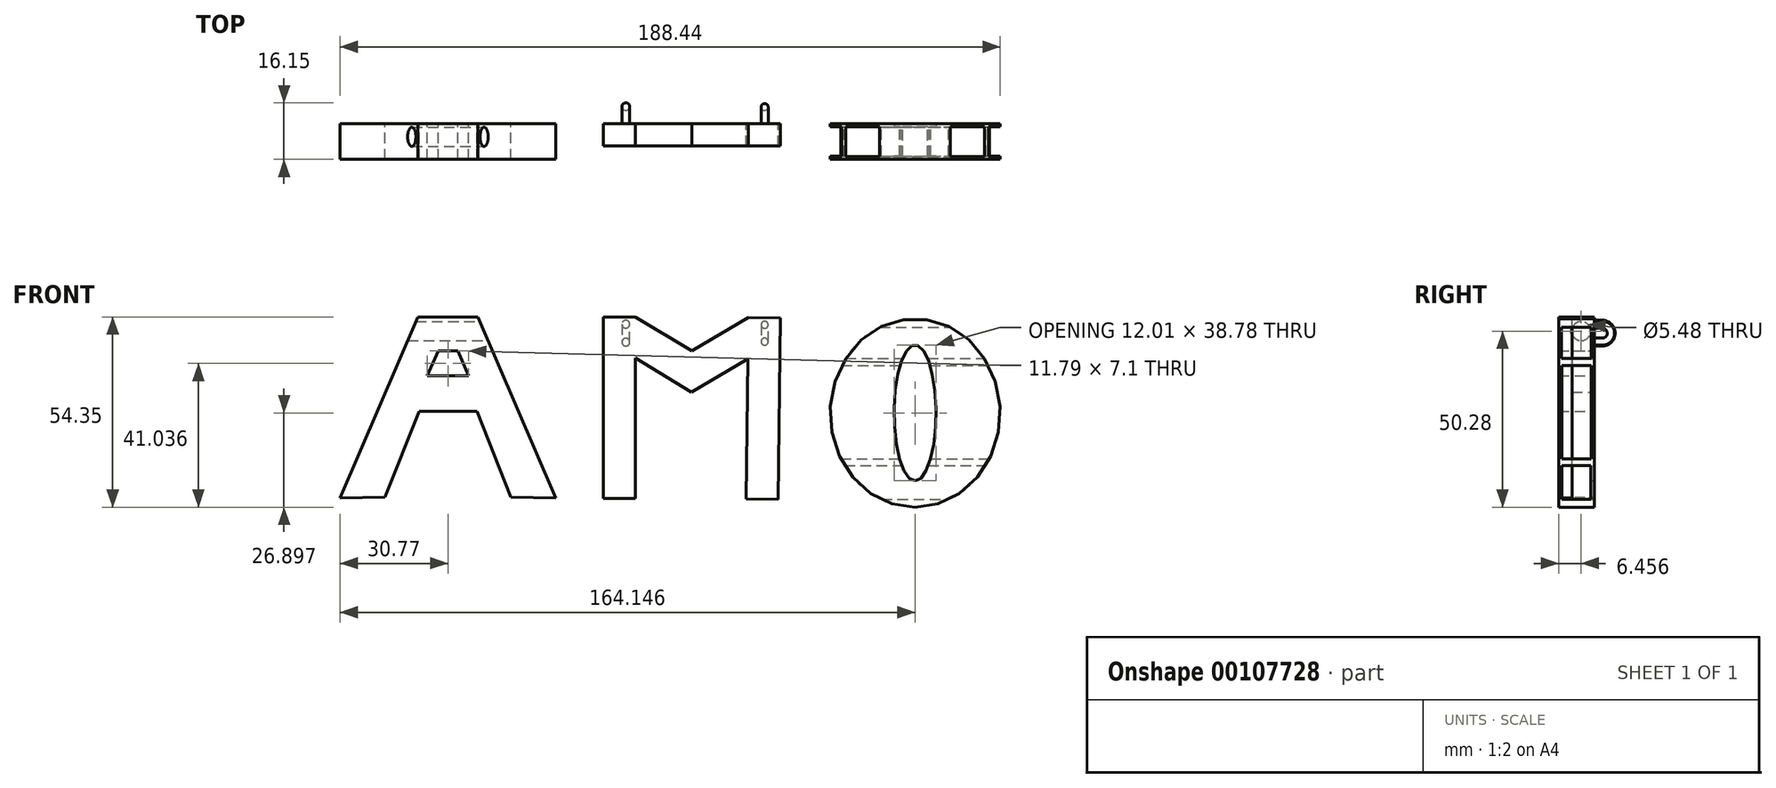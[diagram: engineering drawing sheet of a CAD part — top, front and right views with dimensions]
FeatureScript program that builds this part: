
annotation { "Feature Type Name" : "Feature", "Feature Type Description" : "" }
export const myFeature = defineFeature(function(context is Context, id is Id, definition is map)
    precondition{}
    {
        {
            var Q0;
            Q0=qCreatedBy(makeId("Front.planeOp"),FACE);
            var sketch = newSketch(context, id + "F0", { "sketchPlane" : qUnion([Q0])});
            skLineSegment(sketch, "E0", {"start": v(-8.58, 0) * mm, "end": v(-30.77, -51.77) * mm});
            skLineSegment(sketch, "E1", {"start": v(-30.77, -51.77) * mm, "end": v(-17.99, -51.5) * mm});
            skLineSegment(sketch, "E2", {"start": v(-17.99, -51.5) * mm, "end": v(-8.26, -27.04) * mm});
            skLineSegment(sketch, "E3", {"start": v(-5.9, -16.86) * mm, "end": v(-2.8, -9.76) * mm});
            skLineSegment(sketch, "E4.MirrorCS", {"start": v(30.77, -51.77) * mm, "end": v(17.99, -51.5) * mm});
            skLineSegment(sketch, "E5.MirrorCS", {"start": v(17.99, -51.5) * mm, "end": v(8.26, -27.04) * mm});
            skLineSegment(sketch, "E6.MirrorCS", {"start": v(8.58, 0) * mm, "end": v(30.77, -51.77) * mm});
            skLineSegment(sketch, "E7.MirrorCS", {"start": v(5.9, -16.86) * mm, "end": v(2.8, -9.76) * mm});
            skLineSegment(sketch, "E8", {"start": v(-2.8, -9.76) * mm, "end": v(2.8, -9.76) * mm});
            skLineSegment(sketch, "E9", {"start": v(-5.9, -16.86) * mm, "end": v(5.9, -16.86) * mm});
            skLineSegment(sketch, "E10", {"start": v(-8.26, -27.04) * mm, "end": v(8.26, -27.04) * mm});
            skLineSegment(sketch, "E11", {"start": v(-8.58, 0) * mm, "end": v(8.58, 0) * mm});
            skSolve(sketch);
        }
        {
            var Q0;
            Q0=makeQuery(id+"F0.imprint","IMPRINT",FACE,{"disambiguationData":[TD([[makeQuery(id+"F0.imprint","IMPRINT",EDGE,{"derivedFrom":sQuery(id+"F0.wireOp",EDGE,"E0")}),1.0]])]});
            extrude(context, id + "F1", {"entities" : qUnion([Q0]), "depth" : 10.16 * mm});
        }
        {
            var Q0;
            Q0=qCreatedBy(makeId("Front.planeOp"),FACE);
            var sketch = newSketch(context, id + "F2", { "sketchPlane" : qUnion([Q0])});
            skLineSegment(sketch, "E12.bottom", {"start": v(44.42, -51.8) * mm, "end": v(53.57, -51.8) * mm});
            skLineSegment(sketch, "E12.top", {"start": v(44.42, 0) * mm, "end": v(53.57, 0) * mm});
            skLineSegment(sketch, "E12.left", {"start": v(44.42, -51.8) * mm, "end": v(44.42, 0) * mm});
            skLineSegment(sketch, "E12.right", {"start": v(53.57, -51.8) * mm, "end": v(53.57, -11.8) * mm});
            skLineSegment(sketch, "E13", {"start": v(53.57, -11.8) * mm, "end": v(69.53, -21.5) * mm});
            skLineSegment(sketch, "E14", {"start": v(53.57, 0) * mm, "end": v(69.6, -9.73) * mm});
            skLineSegment(sketch, "E15.MirrorCS", {"start": v(85.72, -0.17) * mm, "end": v(69.6, -9.73) * mm});
            skLineSegment(sketch, "E16.MirrorCS", {"start": v(85.6, -11.96) * mm, "end": v(69.53, -21.5) * mm});
            skLineSegment(sketch, "E17.MirrorCS", {"start": v(94.33, -52.06) * mm, "end": v(85.19, -51.97) * mm});
            skLineSegment(sketch, "E18.MirrorCS", {"start": v(94.87, -0.26) * mm, "end": v(85.72, -0.17) * mm});
            skLineSegment(sketch, "E19.MirrorCS", {"start": v(85.19, -51.97) * mm, "end": v(85.6, -11.96) * mm});
            skLineSegment(sketch, "E20.MirrorCS", {"start": v(94.33, -52.06) * mm, "end": v(94.87, -0.26) * mm});
            skSolve(sketch);
        }
        {
            var Q0;
            Q0=makeQuery(id+"F2.imprint","IMPRINT",FACE,{"disambiguationData":[TD([[makeQuery(id+"F2.imprint","IMPRINT",EDGE,{"derivedFrom":sQuery(id+"F2.wireOp",EDGE,"E12.bottom")}),1.0]])]});
            var Q1;
            Q1 = qSketchRegion(id + "F2", true);
            extrude(context, id + "F3", {"entities" : qUnion([Q0, Q1]), "depth" : 6.35 * mm});
        }
        {
            var Q0;
            Q0=qCreatedBy(makeId("Right.planeOp"),FACE);
            cPlane(context, id + "F4", {"entities" : qUnion([Q0]), "cplaneType" : CPlaneType.OFFSET, "offset" : 69.85 * mm, "width" : 152.4 * mm, "height" : 152.4 * mm});
        }
        {
            var Q0;
            Q0=qCreatedBy(id+"F4.planeOp",FACE);
            cPlane(context, id + "F5", {"entities" : qUnion([Q0]), "cplaneType" : CPlaneType.OFFSET, "offset" : 20.57 * mm, "width" : 152.4 * mm, "height" : 152.4 * mm});
        }
        {
            var Q0;
            Q0=qCreatedBy(id+"F5.planeOp",FACE);
            var sketch = newSketch(context, id + "F6", { "sketchPlane" : qUnion([Q0])});
            skLineSegment(sketch, "E21.bottom", {"start": v(0, -2.27) * mm, "end": v(2.37, -2.27) * mm});
            skLineSegment(sketch, "E21.top", {"start": v(0, -7.07) * mm, "end": v(2.37, -7.07) * mm});
            skArc(sketch, "E22", {"start": v(2.37, -7.07) * mm, "mid": v(4.77, -4.67) * mm, "end": v(2.37, -2.27) * mm});
            skSolve(sketch);
        }
        {
            var Q0;
            Q0=makeQuery(id+"F3.opExtrude","CAP_FACE",FACE,{"disambiguationData":[OSD([sQuery(id+"F2.wireOp",EDGE,"E12.bottom"),sQuery(id+"F2.wireOp",EDGE,"E12.top"),sQuery(id+"F2.wireOp",EDGE,"E12.left"),sQuery(id+"F2.wireOp",EDGE,"E12.right"),sQuery(id+"F2.wireOp",EDGE,"E13"),sQuery(id+"F2.wireOp",EDGE,"E14"),sQuery(id+"F2.wireOp",EDGE,"E15.MirrorCS"),sQuery(id+"F2.wireOp",EDGE,"E16.MirrorCS"),sQuery(id+"F2.wireOp",EDGE,"E17.MirrorCS"),sQuery(id+"F2.wireOp",EDGE,"E18.MirrorCS"),sQuery(id+"F2.wireOp",EDGE,"E19.MirrorCS"),sQuery(id+"F2.wireOp",EDGE,"E20.MirrorCS")])],"isStart":true});
            var sketch = newSketch(context, id + "F7", { "sketchPlane" : qUnion([Q0])});
            skCircle(sketch, "E23", {"center": v(-90.42, -2.27) * mm, "radius": 1.01 * mm});
            skSolve(sketch);
        }
        {
            var Q0;
            Q0 = qSketchRegion(id + "F7", true);
            var Q1;
            Q1 = qConstructionFilter(qBodyType(qCreatedBy(id + "F6" ,EDGE), BodyType.WIRE), ConstructionObject.NO);
            sweep(context, id + "F8", {"operationType" : NewBodyOperationType.ADD, "profiles" : qUnion([Q0]), "path" : qUnion([Q1])});
        }
        {
            var Q0;
            Q0=qCreatedBy(id+"F4.planeOp",FACE);
            cPlane(context, id + "F9", {"entities" : qUnion([Q0]), "cplaneType" : CPlaneType.OFFSET, "offset" : 19.05 * mm, "oppositeDirection" : true, "width" : 152.4 * mm, "height" : 152.4 * mm});
        }
        {
            var Q0;
            Q0=qCreatedBy(id+"F9.planeOp",FACE);
            var sketch = newSketch(context, id + "F10", { "sketchPlane" : qUnion([Q0])});
            skLineSegment(sketch, "E24.bottom", {"start": v(0, -2.1) * mm, "end": v(2.31, -2.1) * mm});
            skLineSegment(sketch, "E24.top", {"start": v(0, -7.2) * mm, "end": v(2.31, -7.2) * mm});
            skArc(sketch, "E25", {"start": v(2.31, -7.2) * mm, "mid": v(4.87, -4.65) * mm, "end": v(2.31, -2.1) * mm});
            skSolve(sketch);
        }
        {
            var Q0;
            Q0=qCreatedBy(makeId("Front.planeOp"),FACE);
            var sketch = newSketch(context, id + "F11", { "sketchPlane" : qUnion([Q0])});
            skCircle(sketch, "E26", {"center": v(50.8, -2.1) * mm, "radius": 1.12 * mm});
            skSolve(sketch);
        }
        {
            var Q0;
            Q0 = qSketchRegion(id + "F11", true);
            var Q1;
            Q1 = qConstructionFilter(qBodyType(qCreatedBy(id + "F10" ,EDGE), BodyType.WIRE), ConstructionObject.NO);
            sweep(context, id + "F12", {"operationType" : NewBodyOperationType.ADD, "profiles" : qUnion([Q0]), "path" : qUnion([Q1])});
        }
        {
            var Q0;
            Q0=qCreatedBy(makeId("Front.planeOp"),FACE);
            var sketch = newSketch(context, id + "F13", { "sketchPlane" : qUnion([Q0])});
            skEllipse(sketch, "E27", {"center": v(133.38, -27.45) * mm, "majorRadius": 26.9 * mm, "minorRadius": 24.3 * mm, "majorAxis": v(0, -1)});
            skEllipse(sketch, "E28", {"center": v(133.38, -27.45) * mm, "majorRadius": 19.39 * mm, "minorRadius": 6 * mm, "majorAxis": v(0, -1)});
            skSolve(sketch);
        }
        {
            var Q0;
            Q0=makeQuery(id+"F13.imprint","IMPRINT",FACE,{"disambiguationData":[TD([[makeQuery(id+"F13.imprint","IMPRINT",EDGE,{"derivedFrom":sQuery(id+"F13.wireOp",EDGE,"E27")}),1.0]])]});
            extrude(context, id + "F14", {"entities" : qUnion([Q0]), "depth" : 10.16 * mm});
        }
        {
            var Q0;
            Q0=qCreatedBy(makeId("Right.planeOp"),FACE);
            cPlane(context, id + "F15", {"entities" : qUnion([Q0]), "cplaneType" : CPlaneType.OFFSET, "offset" : 133.35 * mm, "width" : 152.4 * mm, "height" : 152.4 * mm});
        }
        {
            var Q0;
            Q0=qCreatedBy(makeId("Right.planeOp"),FACE);
            var sketch = newSketch(context, id + "F16", { "sketchPlane" : qUnion([Q0])});
            skCircle(sketch, "E29", {"center": v(-3.7, -4.07) * mm, "radius": 2.74 * mm});
            skSolve(sketch);
        }
        {
            var Q0;
            Q0 = qSketchRegion(id + "F16", true);
            extrude(context, id + "F17", {"entities" : qUnion([Q0]), "operationType" : NewBodyOperationType.REMOVE, "oppositeDirection" : true, "depth" : 25.4 * mm, "hasSecondDirection" : true, "secondDirectionOppositeDirection" : false, "secondDirectionDepth" : 25.4 * mm});
        }
        {
            var Q0;
            Q0=qCreatedBy(id+"F15.planeOp",FACE);
            var sketch = newSketch(context, id + "F18", { "sketchPlane" : qUnion([Q0])});
            skLineSegment(sketch, "E30.bottom", {"start": v(-9.36, -3) * mm, "end": v(-0.8, -3) * mm});
            skLineSegment(sketch, "E30.top", {"start": v(-9.36, -11.91) * mm, "end": v(-0.8, -11.91) * mm});
            skLineSegment(sketch, "E30.left", {"start": v(-9.36, -3) * mm, "end": v(-9.36, -11.91) * mm});
            skLineSegment(sketch, "E30.right", {"start": v(-0.8, -3) * mm, "end": v(-0.8, -11.91) * mm});
            skLineSegment(sketch, "E31.bottom", {"start": v(-9.2, -13.86) * mm, "end": v(-0.8, -13.86) * mm});
            skLineSegment(sketch, "E31.top", {"start": v(-9.2, -40.52) * mm, "end": v(-0.8, -40.52) * mm});
            skLineSegment(sketch, "E31.left", {"start": v(-9.2, -13.86) * mm, "end": v(-9.2, -40.52) * mm});
            skLineSegment(sketch, "E31.right", {"start": v(-0.8, -13.86) * mm, "end": v(-0.8, -40.52) * mm});
            skLineSegment(sketch, "E32.bottom", {"start": v(-9.2, -42.45) * mm, "end": v(-0.96, -42.45) * mm});
            skLineSegment(sketch, "E32.top", {"start": v(-9.2, -52.16) * mm, "end": v(-0.96, -52.16) * mm});
            skLineSegment(sketch, "E32.left", {"start": v(-9.2, -42.45) * mm, "end": v(-9.2, -52.16) * mm});
            skLineSegment(sketch, "E32.right", {"start": v(-0.96, -42.45) * mm, "end": v(-0.96, -52.16) * mm});
            skSolve(sketch);
        }
        {
            var Q0;
            Q0 = qSketchRegion(id + "F18", true);
            extrude(context, id + "F19", {"entities" : qUnion([Q0]), "operationType" : NewBodyOperationType.REMOVE, "oppositeDirection" : true, "depth" : 25.4 * mm, "hasSecondDirection" : true, "secondDirectionOppositeDirection" : false, "secondDirectionDepth" : 25.4 * mm});
        }
    });
